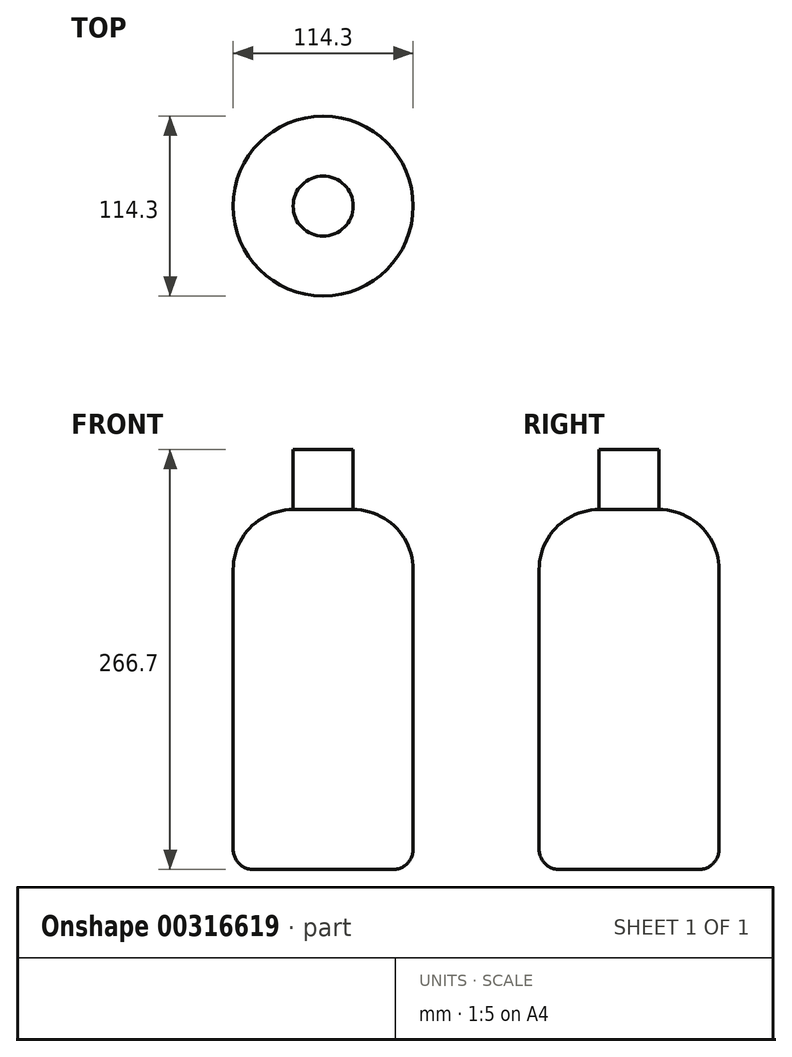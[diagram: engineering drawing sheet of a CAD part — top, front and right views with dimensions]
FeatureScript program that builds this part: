
annotation { "Feature Type Name" : "Feature", "Feature Type Description" : "" }
export const myFeature = defineFeature(function(context is Context, id is Id, definition is map)
    precondition{}
    {
        {
            var Q0;
            Q0=qCreatedBy(makeId("Front.planeOp"),FACE);
            var sketch = newSketch(context, id + "F0", { "sketchPlane" : qUnion([Q0])});
            skLineSegment(sketch, "E0.bottom", {"start": v(-25.63, 203.06) * mm, "end": v(12.47, 203.06) * mm});
            skLineSegment(sketch, "E0.top", {"start": v(-51.03, -25.54) * mm, "end": v(37.87, -25.54) * mm});
            skLineSegment(sketch, "E0.left", {"start": v(-63.73, 164.96) * mm, "end": v(-63.73, -12.84) * mm});
            skLineSegment(sketch, "E0.right", {"start": v(50.57, 164.96) * mm, "end": v(50.57, -12.84) * mm});
            skPoint(sketch, "E1.visualSharp", {"position": v(-63.73, 203.06) * mm});
            skArc(sketch, "E1.filletArc", {"start": v(-25.63, 203.06) * mm, "mid": v(-52.57, 191.9) * mm, "end": v(-63.73, 164.96) * mm});
            skPoint(sketch, "E2.visualSharp", {"position": v(50.57, 203.06) * mm});
            skArc(sketch, "E2.filletArc", {"start": v(50.57, 164.96) * mm, "mid": v(39.41, 191.9) * mm, "end": v(12.47, 203.06) * mm});
            skPoint(sketch, "E3.visualSharp", {"position": v(50.57, -25.54) * mm});
            skArc(sketch, "E3.filletArc", {"start": v(37.87, -25.54) * mm, "mid": v(46.85, -21.82) * mm, "end": v(50.57, -12.84) * mm});
            skPoint(sketch, "E4.visualSharp", {"position": v(-63.73, -25.54) * mm});
            skArc(sketch, "E4.filletArc", {"start": v(-63.73, -12.84) * mm, "mid": v(-60, -21.82) * mm, "end": v(-51.03, -25.54) * mm});
            skLineSegment(sketch, "E5.bottom", {"start": v(-25.63, 241.16) * mm, "end": v(12.47, 241.16) * mm});
            skLineSegment(sketch, "E5.left", {"start": v(-25.63, 241.16) * mm, "end": v(-25.63, 203.06) * mm});
            skLineSegment(sketch, "E5.right", {"start": v(12.47, 241.16) * mm, "end": v(12.47, 203.06) * mm});
            skLineSegment(sketch, "E6", {"start": v(-6.58, 275.34) * mm, "end": v(-6.58, -59.5) * mm});
            skPoint(sketch, "E6.startSnap0", {"position": v(-6.58, 241.16) * mm});
            skPoint(sketch, "E6.endSnap0", {"position": v(-6.58, -25.54) * mm});
            skSolve(sketch);
        }
        {
            var Q0;
            Q0=makeQuery(id+"F0.imprint","IMPRINT",FACE,{"disambiguationData":[TD([[makeQuery(id+"F0.imprint","IMPRINT",EDGE,{"derivedFrom":sQuery(id+"F0.wireOp",EDGE,"E0.right")}),-1.0]])]});
            var Q1;
            {var subQ0=sQuery(id+"F0.wireOp",EDGE,"E5.right");Q1=makeQuery(id+"F0.imprint","IMPRINT",FACE,{"disambiguationData":[TD([[makeQuery(id+"F0.imprint","IMPRINT",EDGE,{"derivedFrom":subQ0}),-1.0]])]});}
            var Q2;
            Q2=sQuery(id+"F0.wireOp",EDGE,"E6");
            revolve(context, id + "F1", {"entities" : qUnion([Q0, Q1]), "axis" : qUnion([Q2]), "revolveType" : RevolveType.FULL});
        }
    });
